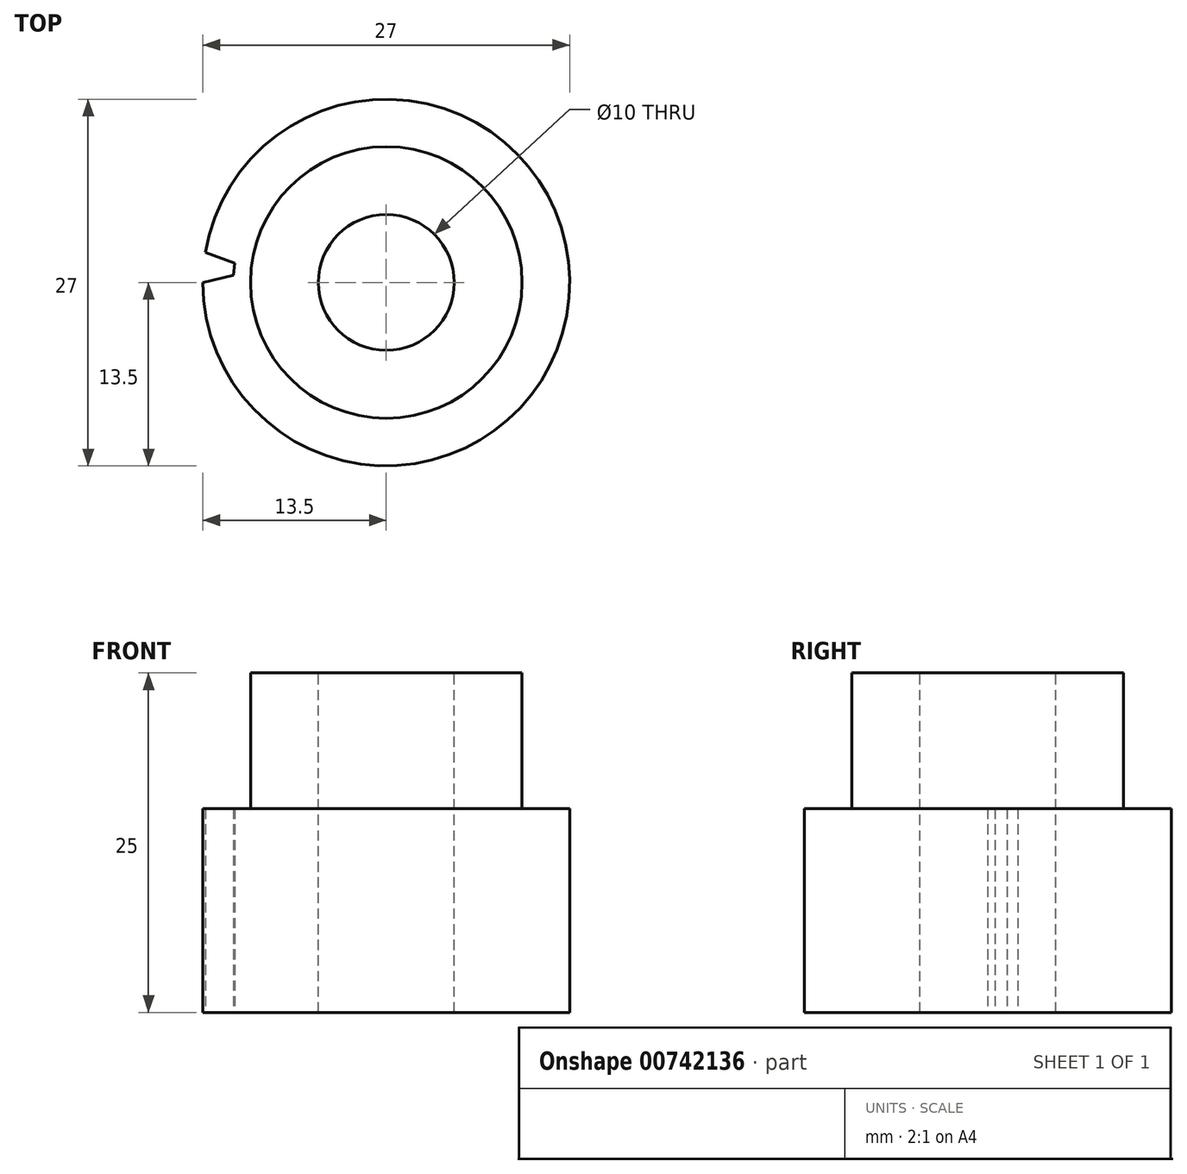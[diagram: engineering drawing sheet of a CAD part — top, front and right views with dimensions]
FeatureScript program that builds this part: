
annotation { "Feature Type Name" : "Feature", "Feature Type Description" : "" }
export const myFeature = defineFeature(function(context is Context, id is Id, definition is map)
    precondition{}
    {
        {
            var Q0;
            Q0=qCreatedBy(makeId("Top.planeOp"),FACE);
            var sketch = newSketch(context, id + "F0", { "sketchPlane" : qUnion([Q0])});
            skCircle(sketch, "E0", {"center": v(0, 0) * mm, "radius": 13.5 * mm});
            skSolve(sketch);
        }
        {
            var Q0;
            Q0 = qSketchRegion(id + "F0", true);
            extrude(context, id + "F1", {"entities" : qUnion([Q0]), "depth" : 15 * mm, "offsetDistance" : 25 * mm});
        }
        {
            var Q0;
            Q0=makeQuery(id+"F1.opExtrude","CAP_FACE",FACE,{"disambiguationData":[OSD([sQuery(id+"F0.wireOp",EDGE,"E0")])],"isStart":false});
            var sketch = newSketch(context, id + "F2", { "sketchPlane" : qUnion([Q0])});
            skCircle(sketch, "E1", {"center": v(0, 0) * mm, "radius": 10 * mm});
            skSolve(sketch);
        }
        {
            var Q0;
            Q0=makeQuery(id+"F2.imprint","IMPRINT",FACE,{"disambiguationData":[TD([[makeQuery(id+"F2.imprint","IMPRINT",EDGE,{"derivedFrom":sQuery(id+"F2.wireOp",EDGE,"E1")}),1.0]])]});
            extrude(context, id + "F3", {"entities" : qUnion([Q0]), "operationType" : NewBodyOperationType.ADD, "depth" : 10 * mm, "offsetDistance" : 25 * mm});
        }
        {
            var Q0;
            Q0=makeQuery(id+"F3.opExtrude","CAP_FACE",FACE,{"disambiguationData":[OSD([sQuery(id+"F2.wireOp",EDGE,"E1")])],"isStart":false});
            var sketch = newSketch(context, id + "F4", { "sketchPlane" : qUnion([Q0])});
            skCircle(sketch, "E2", {"center": v(0, 0) * mm, "radius": 5 * mm});
            skSolve(sketch);
        }
        {
            var Q0;
            Q0 = qSketchRegion(id + "F4", true);
            extrude(context, id + "F5", {"entities" : qUnion([Q0]), "operationType" : NewBodyOperationType.REMOVE, "endBound" : BoundingType.THROUGH_ALL, "oppositeDirection" : true, "depth" : 25 * mm, "offsetDistance" : 25 * mm});
        }
        {
            var Q0;
            Q0=makeQuery(id+"F1.opExtrude","CAP_FACE",FACE,{"disambiguationData":[OSD([sQuery(id+"F0.wireOp",EDGE,"E0")])],"isStart":true});
            var sketch = newSketch(context, id + "F6", { "sketchPlane" : qUnion([Q0])});
            skCircle(sketch, "E3", {"center": v(0, 0) * mm, "radius": 12.5 * mm, "construction": true});
            skCircle(sketch, "E4", {"center": v(0, 0) * mm, "radius": 11.25 * mm, "construction": true});
            skLineSegment(sketch, "E5", {"start": v(0, 0) * mm, "end": v(-13.4, 1.7) * mm, "construction": true});
            skLineSegment(sketch, "E6", {"start": v(0, 0) * mm, "end": v(-13.4, -1.7) * mm, "construction": true});
            skLineSegment(sketch, "E7", {"start": v(-11.16, -1.4) * mm, "end": v(-13.32, -2.2) * mm});
            skLineSegment(sketch, "E8", {"start": v(-11.16, 1.4) * mm, "end": v(-13.45, 1.18) * mm});
            skLineSegment(sketch, "E9", {"start": v(-13.5, 0) * mm, "end": v(-11.24, -0.52) * mm});
            skLineSegment(sketch, "E10", {"start": v(-11.24, -0.52) * mm, "end": v(-11.16, -1.4) * mm});
            skLineSegment(sketch, "E11", {"start": v(-13.5, 0) * mm, "end": v(-13.45, 1.18) * mm});
            skSolve(sketch);
        }
        {
            var Q0;
            {var subQ0=sQuery(id+"F6.wireOp",EDGE,"E7");Q0=makeQuery(id+"F6.imprint","IMPRINT",FACE,{"disambiguationData":[TD([[makeQuery(id+"F6.imprint","IMPRINT",EDGE,{"derivedFrom":subQ0}),-1.0]])]});}
            extrude(context, id + "F7", {"entities" : qUnion([Q0]), "operationType" : NewBodyOperationType.REMOVE, "endBound" : BoundingType.THROUGH_ALL, "oppositeDirection" : true, "depth" : 25 * mm, "offsetDistance" : 25 * mm});
        }
    });
